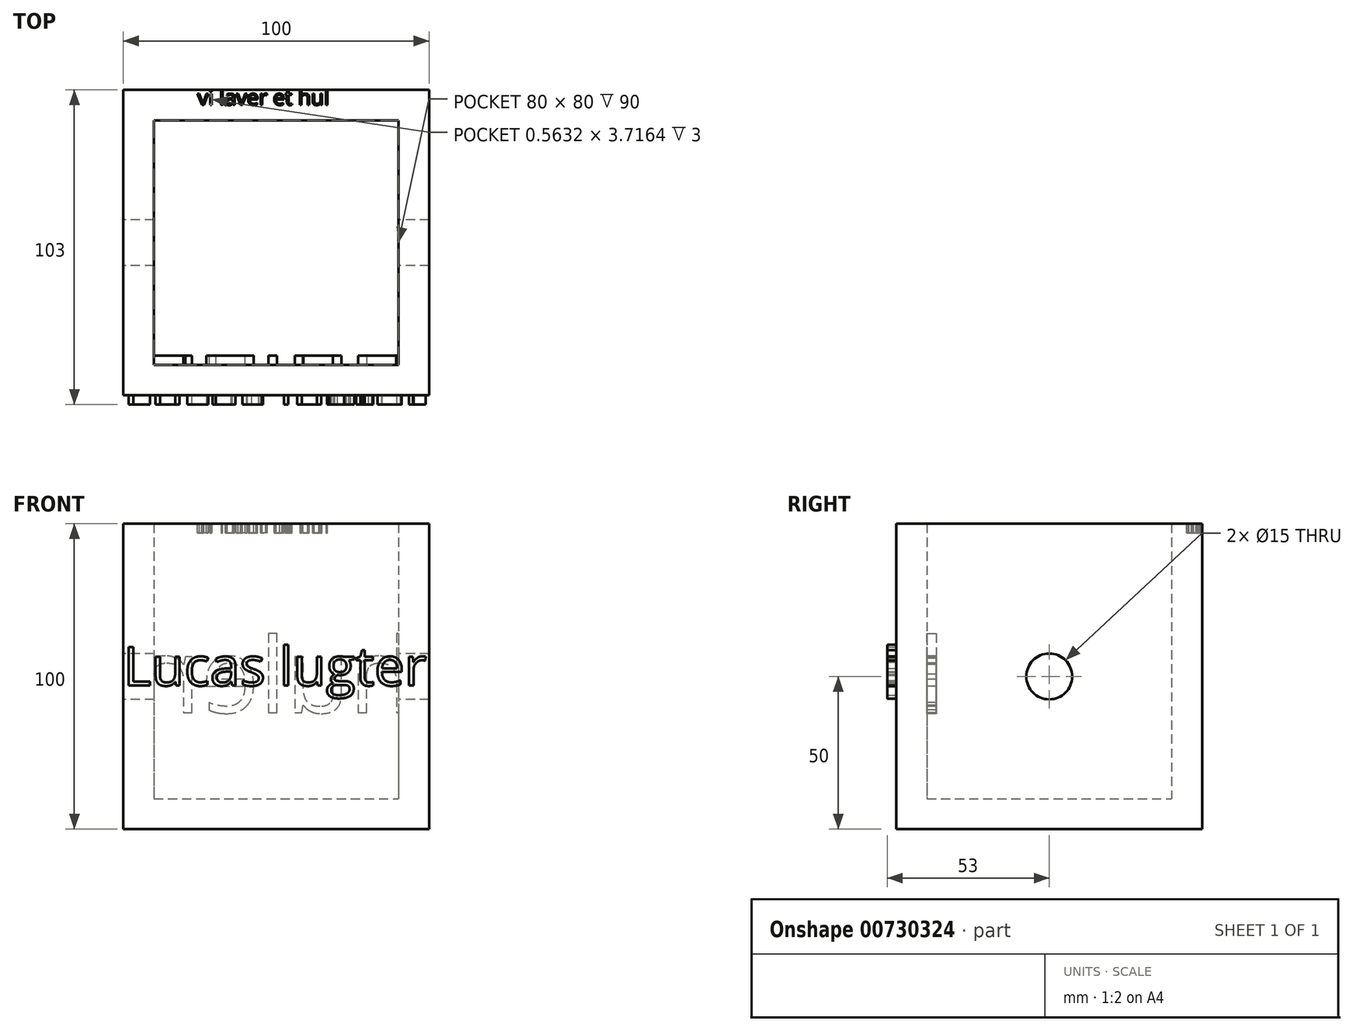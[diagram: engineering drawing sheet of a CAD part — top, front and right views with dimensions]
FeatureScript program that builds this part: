
annotation { "Feature Type Name" : "Feature", "Feature Type Description" : "" }
export const myFeature = defineFeature(function(context is Context, id is Id, definition is map)
    precondition{}
    {
        {
            var Q0;
            Q0=qCreatedBy(makeId("Top.planeOp"),FACE);
            var sketch = newSketch(context, id + "F0", { "sketchPlane" : qUnion([Q0])});
            skLineSegment(sketch, "E0.bottom", {"start": v(0, 0) * mm, "end": v(100, 0) * mm});
            skLineSegment(sketch, "E0.top", {"start": v(0, 100) * mm, "end": v(100, 100) * mm});
            skLineSegment(sketch, "E0.left", {"start": v(0, 0) * mm, "end": v(0, 100) * mm});
            skLineSegment(sketch, "E0.right", {"start": v(100, 0) * mm, "end": v(100, 100) * mm});
            skSolve(sketch);
        }
        {
            var Q0;
            Q0 = qSketchRegion(id + "F0", true);
            extrude(context, id + "F1", {"entities" : qUnion([Q0]), "depth" : 100 * mm, "offsetDistance" : 25 * mm});
        }
        {
            var Q0;
            Q0=makeQuery(id+"F1.opExtrude","CAP_FACE",FACE,{"disambiguationData":[OSD([sQuery(id+"F0.wireOp",EDGE,"E0.bottom"),sQuery(id+"F0.wireOp",EDGE,"E0.top"),sQuery(id+"F0.wireOp",EDGE,"E0.left"),sQuery(id+"F0.wireOp",EDGE,"E0.right")])],"isStart":false});
            shell(context, id + "F2", {"entities" : qUnion([Q0]), "thickness" : 10 * mm});
        }
        {
            var Q0;
            Q0=makeQuery(id+"F1.opExtrude","SWEPT_FACE",FACE,{"disambiguationData":[OSD([sQuery(id+"F0.wireOp",EDGE,"E0.left")])]});
            var sketch = newSketch(context, id + "F3", { "sketchPlane" : qUnion([Q0])});
            skCircle(sketch, "E1", {"center": v(-50, 50) * mm, "radius": 7.5 * mm});
            skSolve(sketch);
        }
        {
            var Q0;
            Q0 = qSketchRegion(id + "F3", true);
            extrude(context, id + "F4", {"entities" : qUnion([Q0]), "operationType" : NewBodyOperationType.REMOVE, "oppositeDirection" : true, "depth" : 100000 * mm, "offsetDistance" : 25 * mm});
        }
        {
            var Q0;
            Q0=makeQuery(id+"F1.opExtrude","SWEPT_FACE",FACE,{"disambiguationData":[OSD([sQuery(id+"F0.wireOp",EDGE,"E0.bottom")])]});
            var sketch = newSketch(context, id + "F5", { "sketchPlane" : qUnion([Q0])});
            skText(sketch, "E2", { "text": "Lucas lugter\n", "fontName": "OpenSans-Regular.ttf"});
            const initialGuessF5  = {"E2": [0, 0.047, 1, 0, 0.01266]};
            skSetInitialGuess(sketch, initialGuessF5);
            skSolve(sketch);
        }
        {
            var Q0;
            Q0 = qSketchRegion(id + "F5", true);
            extrude(context, id + "F6", {"entities" : qUnion([Q0]), "operationType" : NewBodyOperationType.ADD, "depth" : 3 * mm, "offsetDistance" : 25 * mm});
        }
        {
            var Q0;
            Q0=makeQuery(id+"F2.opShell","OFFSET_FACE",FACE,{"disambiguationData":[OSD([sQuery(id+"F0.wireOp",EDGE,"E0.bottom")])]});
            var sketch = newSketch(context, id + "F7", { "sketchPlane" : qUnion([Q0])});
            skText(sketch, "E3", { "text": "hulen", "fontName": "OpenSans-Regular.ttf"});
            const initialGuessF7  = {"E3": [-0.095, 0.03815, 1, 0, 0.02455]};
            skSetInitialGuess(sketch, initialGuessF7);
            skSolve(sketch);
        }
        {
            var Q0;
            Q0 = qSketchRegion(id + "F7", true);
            extrude(context, id + "F8", {"entities" : qUnion([Q0]), "operationType" : NewBodyOperationType.ADD, "depth" : 3 * mm, "offsetDistance" : 25 * mm});
        }
        {
            var Q0;
            Q0=makeQuery(id+"F1.opExtrude","CAP_FACE",FACE,{"disambiguationData":[OSD([sQuery(id+"F0.wireOp",EDGE,"E0.bottom"),sQuery(id+"F0.wireOp",EDGE,"E0.top"),sQuery(id+"F0.wireOp",EDGE,"E0.left"),sQuery(id+"F0.wireOp",EDGE,"E0.right")])],"isStart":false});
            var sketch = newSketch(context, id + "F9", { "sketchPlane" : qUnion([Q0])});
            skText(sketch, "E4", { "text": "vi laver et hul", "fontName": "OpenSans-Regular.ttf"});
            const initialGuessF9  = {"E4": [0.02426, 0.095, 1, 0, 0.005]};
            skSetInitialGuess(sketch, initialGuessF9);
            skSolve(sketch);
        }
        {
            var Q0;
            Q0 = qSketchRegion(id + "F9", true);
            extrude(context, id + "F10", {"entities" : qUnion([Q0]), "operationType" : NewBodyOperationType.REMOVE, "oppositeDirection" : true, "depth" : 3 * mm, "offsetDistance" : 25 * mm});
        }
    });
